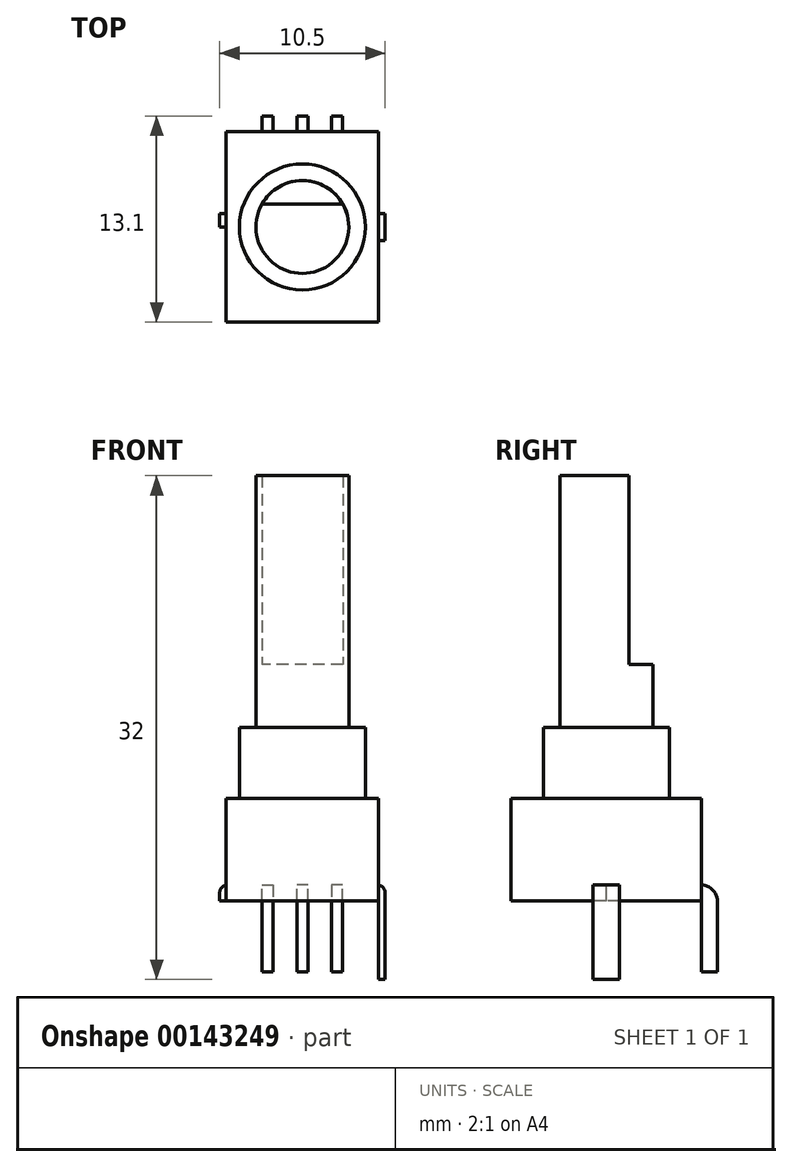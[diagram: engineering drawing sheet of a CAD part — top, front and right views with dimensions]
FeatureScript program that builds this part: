
annotation { "Feature Type Name" : "Feature", "Feature Type Description" : "" }
export const myFeature = defineFeature(function(context is Context, id is Id, definition is map)
    precondition{}
    {
        {
            var Q0;
            Q0=qCreatedBy(makeId("Top.planeOp"),FACE);
            var sketch = newSketch(context, id + "F0", { "sketchPlane" : qUnion([Q0])});
            skLineSegment(sketch, "E0.bottom", {"start": v(-34.74, 14.95) * mm, "end": v(-25.04, 14.95) * mm});
            skLineSegment(sketch, "E0.top", {"start": v(-34.74, 2.85) * mm, "end": v(-25.04, 2.85) * mm});
            skLineSegment(sketch, "E0.left", {"start": v(-34.74, 14.95) * mm, "end": v(-34.74, 2.85) * mm});
            skLineSegment(sketch, "E0.right", {"start": v(-25.04, 14.95) * mm, "end": v(-25.04, 2.85) * mm});
            skPoint(sketch, "E1", {"position": v(-29.9, 8.9) * mm});
            skPoint(sketch, "E1.positionSnap0", {"position": v(-34.74, 8.9) * mm});
            skPoint(sketch, "E1.positionSnap1", {"position": v(-29.9, 14.95) * mm});
            skCircle(sketch, "E2", {"center": v(-29.9, 8.9) * mm, "radius": 4 * mm});
            skSolve(sketch);
        }
        {
            var Q0;
            Q0=makeQuery(id+"F0.imprint","IMPRINT",FACE,{"disambiguationData":[TD([[makeQuery(id+"F0.imprint","IMPRINT",EDGE,{"derivedFrom":sQuery(id+"F0.wireOp",EDGE,"E0.bottom")}),-1.0]])]});
            var Q1;
            Q1=makeQuery(id+"F0.imprint","IMPRINT",FACE,{"disambiguationData":[TD([[makeQuery(id+"F0.imprint","IMPRINT",EDGE,{"derivedFrom":sQuery(id+"F0.wireOp",EDGE,"E2")}),1.0]])]});
            extrude(context, id + "F1", {"entities" : qUnion([Q0, Q1]), "oppositeDirection" : true, "depth" : 6.5 * mm});
        }
        {
            var Q0;
            Q0=makeQuery(id+"F0.imprint","IMPRINT",FACE,{"disambiguationData":[TD([[makeQuery(id+"F0.imprint","IMPRINT",EDGE,{"derivedFrom":sQuery(id+"F0.wireOp",EDGE,"E2")}),1.0]])]});
            extrude(context, id + "F2", {"entities" : qUnion([Q0]), "operationType" : NewBodyOperationType.ADD, "depth" : 4.5 * mm});
        }
        {
            var Q0;
            Q0=makeQuery(id+"F2.opExtrude","CAP_FACE",FACE,{"disambiguationData":[OSD([sQuery(id+"F0.wireOp",EDGE,"E2")])],"isStart":false});
            var sketch = newSketch(context, id + "F3", { "sketchPlane" : qUnion([Q0])});
            skPoint(sketch, "E3.0", {"position": v(-29.9, 8.9) * mm});
            skCircle(sketch, "E4", {"center": v(-29.9, 8.9) * mm, "radius": 2.95 * mm});
            skLineSegment(sketch, "E5", {"start": v(-29.9, 5.95) * mm, "end": v(-29.9, 10.35) * mm});
            skLineSegment(sketch, "E6", {"start": v(-27.32, 10.35) * mm, "end": v(-32.46, 10.35) * mm});
            skSolve(sketch);
        }
        {
            var Q0;
            {var subQ0=sQuery(id+"F3.wireOp",EDGE,"E5");Q0=makeQuery(id+"F3.imprint","IMPRINT",FACE,{"disambiguationData":[TD([[makeQuery(id+"F3.imprint","IMPRINT",EDGE,{"derivedFrom":subQ0}),1.0]])]});}
            var Q1;
            {var subQ0=sQuery(id+"F3.wireOp",EDGE,"E5");Q1=makeQuery(id+"F3.imprint","IMPRINT",FACE,{"disambiguationData":[TD([[makeQuery(id+"F3.imprint","IMPRINT",EDGE,{"derivedFrom":subQ0}),-1.0]])]});}
            extrude(context, id + "F4", {"entities" : qUnion([Q0, Q1]), "operationType" : NewBodyOperationType.ADD, "depth" : 16 * mm});
        }
        {
            var Q0;
            {var subQ0=sQuery(id+"F3.wireOp",EDGE,"E6");var subQ1=sQuery(id+"F3.wireOp",EDGE,"E4");var subQ2=makeQuery(id+"F3.imprint","INTERSECT",VERTEX,{"disambiguationData":[OD(0.0)],"derivedFrom":[subQ1,subQ0]});Q0=makeQuery(id+"F3.imprint","IMPRINT",FACE,{"disambiguationData":[TD([[makeQuery(id+"F3.imprint","IMPRINT",EDGE,{"disambiguationData":[TD([[subQ2,-1.0]])],"derivedFrom":subQ1}),1.0]])]});}
            extrude(context, id + "F5", {"entities" : qUnion([Q0]), "operationType" : NewBodyOperationType.ADD, "depth" : 4 * mm});
        }
        {
            var Q0;
            Q0=makeQuery(id+"F1.opExtrude","SWEPT_FACE",FACE,{"disambiguationData":[OSD([sQuery(id+"F0.wireOp",EDGE,"E0.bottom")])]});
            var sketch = newSketch(context, id + "F6", { "sketchPlane" : qUnion([Q0])});
            skLineSegment(sketch, "E7.0", {"start": v(34.74, -6.5) * mm, "end": v(25.04, -6.5) * mm});
            skLineSegment(sketch, "E8.0", {"start": v(25.04, -6.5) * mm, "end": v(25.04, 0) * mm});
            skLineSegment(sketch, "E9.0", {"start": v(34.74, 0) * mm, "end": v(25.04, 0) * mm});
            skLineSegment(sketch, "E10.0", {"start": v(34.74, -6.5) * mm, "end": v(34.74, 0) * mm});
            skLineSegment(sketch, "E11", {"start": v(29.9, -6.5) * mm, "end": v(29.9, 0) * mm});
            skLineSegment(sketch, "E12", {"start": v(29.9, -6.5) * mm, "end": v(30.24, -6.5) * mm});
            skLineSegment(sketch, "E13", {"start": v(30.24, -6.5) * mm, "end": v(29.54, -6.5) * mm});
            skLineSegment(sketch, "E14", {"start": v(29.54, -6.5) * mm, "end": v(29.54, -11) * mm});
            skLineSegment(sketch, "E15.bottom", {"start": v(29.54, -11) * mm, "end": v(30.24, -11) * mm});
            skLineSegment(sketch, "E15.top", {"start": v(29.54, -6.5) * mm, "end": v(30.24, -6.5) * mm});
            skLineSegment(sketch, "E15.left", {"start": v(29.54, -11) * mm, "end": v(29.54, -6.5) * mm});
            skLineSegment(sketch, "E15.right", {"start": v(30.24, -11) * mm, "end": v(30.24, -6.5) * mm});
            skLineSegment(sketch, "E16.top", {"start": v(29.54, -5.5) * mm, "end": v(30.24, -5.5) * mm});
            skLineSegment(sketch, "E16.left", {"start": v(29.54, -6.5) * mm, "end": v(29.54, -5.5) * mm});
            skLineSegment(sketch, "E16.right", {"start": v(30.24, -6.5) * mm, "end": v(30.24, -5.5) * mm});
            skLineSegment(sketch, "E17", {"start": v(29.54, -5.5) * mm, "end": v(28.04, -5.5) * mm, "construction": true});
            skLineSegment(sketch, "E18", {"start": v(28.04, -5.5) * mm, "end": v(28.04, -11) * mm});
            skLineSegment(sketch, "E19", {"start": v(28.04, -11) * mm, "end": v(27.34, -11) * mm});
            skLineSegment(sketch, "E20", {"start": v(27.34, -11) * mm, "end": v(27.34, -5.5) * mm});
            skLineSegment(sketch, "E21", {"start": v(27.34, -5.5) * mm, "end": v(28.04, -5.5) * mm});
            skLineSegment(sketch, "E22.MirrorCS", {"start": v(32.44, -11) * mm, "end": v(32.44, -5.5) * mm});
            skLineSegment(sketch, "E23.MirrorCS", {"start": v(31.74, -5.5) * mm, "end": v(31.74, -11) * mm});
            skLineSegment(sketch, "E24.MirrorCS", {"start": v(32.44, -5.5) * mm, "end": v(31.74, -5.5) * mm});
            skLineSegment(sketch, "E25.MirrorCS", {"start": v(31.74, -11) * mm, "end": v(32.44, -11) * mm});
            skSolve(sketch);
        }
        {
            var Q0;
            {var subQ5=sQuery(id+"F6.wireOp",EDGE,"E19");Q0=makeQuery(id+"F6.imprint","IMPRINT",FACE,{"disambiguationData":[TD([[makeQuery(id+"F6.imprint","IMPRINT",EDGE,{"derivedFrom":subQ5}),-1.0]])]});}
            var Q1;
            {var subQ5=sQuery(id+"F6.wireOp",EDGE,"E21");Q1=makeQuery(id+"F6.imprint","IMPRINT",FACE,{"disambiguationData":[TD([[makeQuery(id+"F6.imprint","IMPRINT",EDGE,{"derivedFrom":subQ5}),-1.0]])]});}
            var Q2;
            {var subQ5=sQuery(id+"F6.wireOp",EDGE,"E16.left");Q2=makeQuery(id+"F6.imprint","IMPRINT",FACE,{"disambiguationData":[TD([[makeQuery(id+"F6.imprint","IMPRINT",EDGE,{"derivedFrom":subQ5}),-1.0]])]});}
            var Q3;
            {var subQ5=sQuery(id+"F6.wireOp",EDGE,"E16.right");Q3=makeQuery(id+"F6.imprint","IMPRINT",FACE,{"disambiguationData":[TD([[makeQuery(id+"F6.imprint","IMPRINT",EDGE,{"derivedFrom":subQ5}),1.0]])]});}
            var Q4;
            Q4=makeQuery(id+"F6.imprint","IMPRINT",FACE,{"disambiguationData":[TD([[makeQuery(id+"F6.imprint","IMPRINT",EDGE,{"derivedFrom":sQuery(id+"F6.wireOp",EDGE,"E15.bottom")}),1.0]])]});
            var Q5;
            {var subQ5=sQuery(id+"F6.wireOp",EDGE,"E24.MirrorCS");Q5=makeQuery(id+"F6.imprint","IMPRINT",FACE,{"disambiguationData":[TD([[makeQuery(id+"F6.imprint","IMPRINT",EDGE,{"derivedFrom":subQ5}),1.0]])]});}
            var Q6;
            {var subQ5=sQuery(id+"F6.wireOp",EDGE,"E25.MirrorCS");Q6=makeQuery(id+"F6.imprint","IMPRINT",FACE,{"disambiguationData":[TD([[makeQuery(id+"F6.imprint","IMPRINT",EDGE,{"derivedFrom":subQ5}),1.0]])]});}
            extrude(context, id + "F7", {"entities" : qUnion([Q0, Q1, Q2, Q3, Q4, Q5, Q6]), "operationType" : NewBodyOperationType.ADD, "depth" : 1 * mm});
        }
        {
            var Q0;
            Q0=makeQuery(id+"F7.opExtrude","CAP_EDGE",EDGE,{"disambiguationData":[OSD([sQuery(id+"F6.wireOp",EDGE,"E21")])],"isStart":false});
            var Q1;
            Q1=makeQuery(id+"F7.opExtrude","CAP_EDGE",EDGE,{"disambiguationData":[OSD([sQuery(id+"F6.wireOp",EDGE,"E16.top")])],"isStart":false});
            var Q2;
            Q2=makeQuery(id+"F7.opExtrude","CAP_EDGE",EDGE,{"disambiguationData":[OSD([sQuery(id+"F6.wireOp",EDGE,"E24.MirrorCS")])],"isStart":false});
            fillet(context, id + "F8", {"entities" : qUnion([Q0, Q1, Q2]), "radius" : 1 * mm, "tangentPropagation" : true, "allowEdgeOverflow" : false});
        }
        {
            var Q0;
            Q0=makeQuery(id+"F1.opExtrude","SWEPT_FACE",FACE,{"disambiguationData":[OSD([sQuery(id+"F0.wireOp",EDGE,"E0.right")])]});
            var sketch = newSketch(context, id + "F9", { "sketchPlane" : qUnion([Q0])});
            skLineSegment(sketch, "E26", {"start": v(8.9, -6.5) * mm, "end": v(8.9, 0) * mm});
            skLineSegment(sketch, "E27.0", {"start": v(14.95, -6.5) * mm, "end": v(2.85, -6.5) * mm});
            skLineSegment(sketch, "E28.0", {"start": v(2.85, -6.5) * mm, "end": v(2.85, 0) * mm});
            skLineSegment(sketch, "E29.0", {"start": v(14.95, 0) * mm, "end": v(2.85, 0) * mm});
            skLineSegment(sketch, "E30.0", {"start": v(14.95, -6.5) * mm, "end": v(14.95, 0) * mm});
            skLineSegment(sketch, "E31", {"start": v(8.9, -6.5) * mm, "end": v(9.75, -6.5) * mm});
            skLineSegment(sketch, "E32", {"start": v(9.75, -6.5) * mm, "end": v(9.75, -11.5) * mm});
            skLineSegment(sketch, "E33.MirrorCS", {"start": v(8.9, -6.5) * mm, "end": v(8.05, -6.5) * mm});
            skLineSegment(sketch, "E34.MirrorCS", {"start": v(2.85, -6.5) * mm, "end": v(14.95, -6.5) * mm});
            skLineSegment(sketch, "E35.MirrorCS", {"start": v(8.05, -6.5) * mm, "end": v(8.05, -11.5) * mm});
            skLineSegment(sketch, "E36", {"start": v(8.05, -6.5) * mm, "end": v(8.05, -5.5) * mm});
            skLineSegment(sketch, "E37.bottom", {"start": v(8.05, -5.5) * mm, "end": v(9.75, -5.5) * mm});
            skLineSegment(sketch, "E37.top", {"start": v(8.05, -11.5) * mm, "end": v(9.75, -11.5) * mm});
            skLineSegment(sketch, "E37.left", {"start": v(8.05, -5.5) * mm, "end": v(8.05, -11.5) * mm});
            skLineSegment(sketch, "E37.right", {"start": v(9.75, -5.5) * mm, "end": v(9.75, -11.5) * mm});
            skSolve(sketch);
        }
        {
            var Q0;
            {var subQ0=sQuery(id+"F9.wireOp",EDGE,"E34.MirrorCS");var subQ1=sQuery(id+"F9.wireOp",EDGE,"E26");var subQ2=makeQuery(id+"F9.imprint","INTERSECT",VERTEX,{"derivedFrom":[subQ1,subQ0]});Q0=makeQuery(id+"F9.imprint","IMPRINT",FACE,{"disambiguationData":[TD([[makeQuery(id+"F9.imprint","IMPRINT",EDGE,{"disambiguationData":[TD([[subQ2,-1.0]])],"derivedFrom":subQ1}),1.0]])]});}
            var Q1;
            {var subQ0=sQuery(id+"F9.wireOp",EDGE,"E34.MirrorCS");var subQ1=sQuery(id+"F9.wireOp",EDGE,"E26");var subQ2=makeQuery(id+"F9.imprint","INTERSECT",VERTEX,{"derivedFrom":[subQ1,subQ0]});Q1=makeQuery(id+"F9.imprint","IMPRINT",FACE,{"disambiguationData":[TD([[makeQuery(id+"F9.imprint","IMPRINT",EDGE,{"disambiguationData":[TD([[subQ2,-1.0]])],"derivedFrom":subQ1}),-1.0]])]});}
            var Q2;
            {var subQ1=sQuery(id+"F9.wireOp",EDGE,"E37.top");Q2=makeQuery(id+"F9.imprint","IMPRINT",FACE,{"disambiguationData":[TD([[makeQuery(id+"F9.imprint","IMPRINT",EDGE,{"derivedFrom":subQ1}),1.0]])]});}
            extrude(context, id + "F10", {"entities" : qUnion([Q0, Q1, Q2]), "operationType" : NewBodyOperationType.ADD, "depth" : .4 * mm});
        }
        {
            var Q0;
            Q0=makeQuery(id+"F10.opExtrude","CAP_EDGE",EDGE,{"disambiguationData":[OSD([sQuery(id+"F9.wireOp",EDGE,"E37.bottom")])],"isStart":false});
            fillet(context, id + "F11", {"entities" : qUnion([Q0]), "radius" : .5 * mm, "tangentPropagation" : true, "allowEdgeOverflow" : false});
        }
        {
            var Q0;
            Q0=makeQuery(id+"F1.opExtrude","SWEPT_FACE",FACE,{"disambiguationData":[OSD([sQuery(id+"F0.wireOp",EDGE,"E0.left")])]});
            var sketch = newSketch(context, id + "F12", { "sketchPlane" : qUnion([Q0])});
            skLineSegment(sketch, "E38.0", {"start": v(-14.95, -6.5) * mm, "end": v(-14.95, 0) * mm});
            skLineSegment(sketch, "E39.0", {"start": v(-14.95, 0) * mm, "end": v(-2.85, 0) * mm});
            skLineSegment(sketch, "E40.0", {"start": v(-14.95, -6.5) * mm, "end": v(-2.85, -6.5) * mm});
            skLineSegment(sketch, "E41.0", {"start": v(-2.85, -6.5) * mm, "end": v(-2.85, 0) * mm});
            skLineSegment(sketch, "E42", {"start": v(-8.9, -6.5) * mm, "end": v(-8.9, 0) * mm});
            skLineSegment(sketch, "E43", {"start": v(-8.9, -6.5) * mm, "end": v(-8.05, -6.5) * mm});
            skLineSegment(sketch, "E44.0", {"start": v(-9.75, -6.5) * mm, "end": v(-9.75, -11.5) * mm});
            skLineSegment(sketch, "E45.0", {"start": v(-8.05, -6.5) * mm, "end": v(-8.05, -11.5) * mm});
            skLineSegment(sketch, "E46.0", {"start": v(-8.05, -11.5) * mm, "end": v(-9.75, -11.5) * mm});
            skLineSegment(sketch, "E47", {"start": v(-8.05, -6.5) * mm, "end": v(-8.05, -5.5) * mm});
            skLineSegment(sketch, "E48.bottom", {"start": v(-8.05, -5.5) * mm, "end": v(-9.75, -5.5) * mm});
            skLineSegment(sketch, "E48.left", {"start": v(-8.05, -5.5) * mm, "end": v(-8.05, -11.5) * mm});
            skLineSegment(sketch, "E48.right", {"start": v(-9.75, -5.5) * mm, "end": v(-9.75, -11.5) * mm});
            skSolve(sketch);
        }
        {
            var Q0;
            {var subQ3=sQuery(id+"F12.wireOp",EDGE,"E48.right");var subQ5=sQuery(id+"F12.wireOp",EDGE,"E48.bottom");var subQ7=makeQuery(id+"F12.imprint","INTERSECT",VERTEX,{"derivedFrom":[subQ5,subQ3]});Q0=makeQuery(id+"F12.imprint","IMPRINT",FACE,{"disambiguationData":[TD([[makeQuery(id+"F12.imprint","IMPRINT",EDGE,{"disambiguationData":[TD([[subQ7,1.0]])],"derivedFrom":subQ5}),1.0]])]});}
            var Q1;
            {var subQ0=sQuery(id+"F12.wireOp",EDGE,"E43");Q1=makeQuery(id+"F12.imprint","IMPRINT",FACE,{"disambiguationData":[TD([[makeQuery(id+"F12.imprint","IMPRINT",EDGE,{"derivedFrom":subQ0}),1.0]])]});}
            var Q2;
            {var subQ1=sQuery(id+"F12.wireOp",EDGE,"E43");Q2=makeQuery(id+"F12.imprint","IMPRINT",FACE,{"disambiguationData":[TD([[makeQuery(id+"F12.imprint","IMPRINT",EDGE,{"derivedFrom":subQ1}),-1.0]])]});}
            extrude(context, id + "F13", {"entities" : qUnion([Q0, Q1, Q2]), "operationType" : NewBodyOperationType.ADD, "depth" : .4 * mm});
        }
        {
            var Q0;
            Q0=makeQuery(id+"F13.opExtrude","CAP_EDGE",EDGE,{"disambiguationData":[OSD([sQuery(id+"F12.wireOp",EDGE,"E48.bottom")])],"isStart":false});
            fillet(context, id + "F14", {"entities" : qUnion([Q0]), "radius" : .5 * mm, "tangentPropagation" : true, "allowEdgeOverflow" : false});
        }
    });
